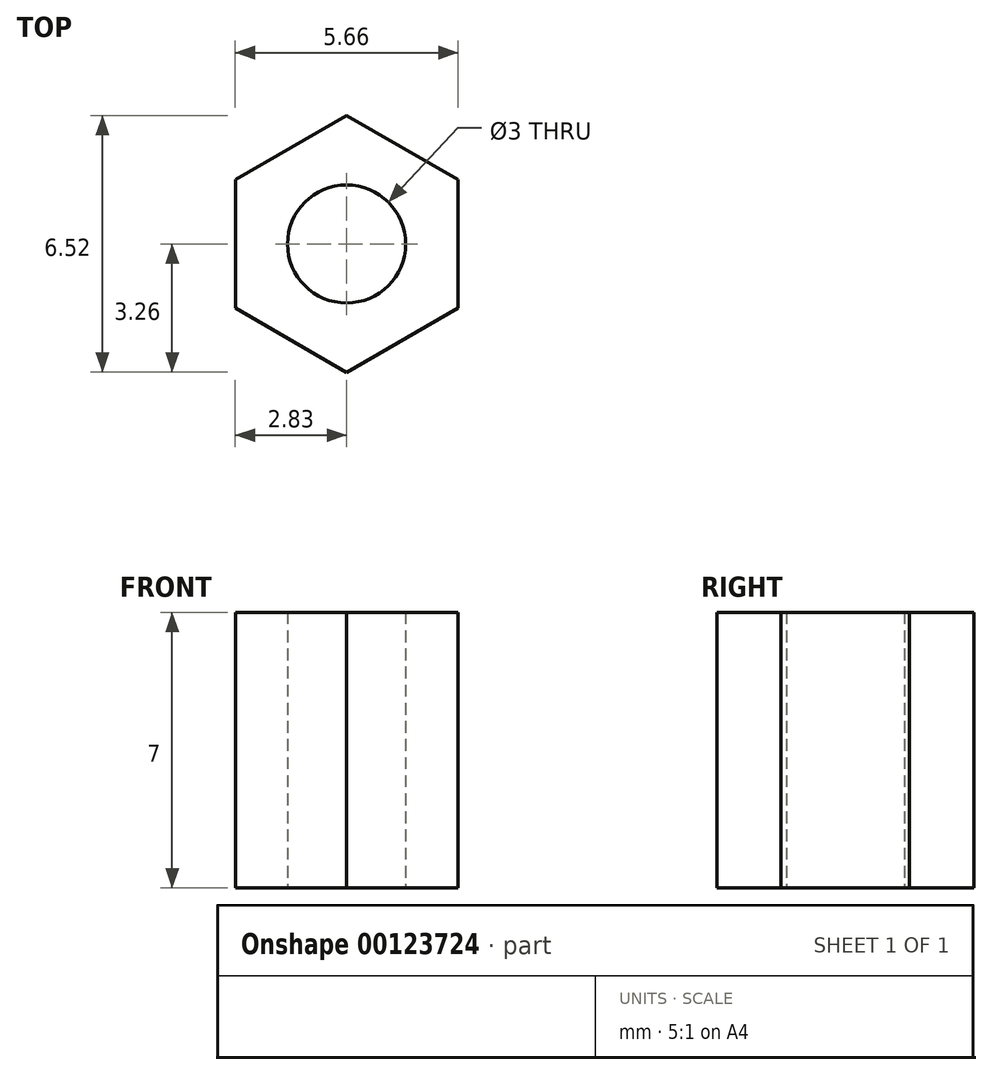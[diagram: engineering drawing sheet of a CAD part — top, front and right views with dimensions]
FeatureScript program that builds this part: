
annotation { "Feature Type Name" : "Feature", "Feature Type Description" : "" }
export const myFeature = defineFeature(function(context is Context, id is Id, definition is map)
    precondition{}
    {
        {
            var Q0;
            Q0=qCreatedBy(makeId("Top.planeOp"),FACE);
            var sketch = newSketch(context, id + "F0", { "sketchPlane" : qUnion([Q0])});
            skCircle(sketch, "E0.cCircle", {"center": v(0, 0) * mm, "radius": 2.83 * mm, "construction": true});
            skLineSegment(sketch, "E0.0", {"start": v(2.83, 1.63) * mm, "end": v(2.83, -1.63) * mm});
            skLineSegment(sketch, "E0.1", {"start": v(2.83, -1.63) * mm, "end": v(0, -3.26) * mm});
            skLineSegment(sketch, "E0.2", {"start": v(0, -3.26) * mm, "end": v(-2.82, -1.63) * mm});
            skLineSegment(sketch, "E0.3", {"start": v(-2.82, -1.63) * mm, "end": v(-2.83, 1.63) * mm});
            skLineSegment(sketch, "E0.4", {"start": v(-2.83, 1.63) * mm, "end": v(0, 3.26) * mm});
            skLineSegment(sketch, "E0.5", {"start": v(0, 3.26) * mm, "end": v(2.83, 1.63) * mm});
            skPoint(sketch, "E0.0.midPoint", {"position": v(2.83, 0) * mm});
            skCircle(sketch, "E1", {"center": v(0, 0) * mm, "radius": 1.5 * mm});
            skSolve(sketch);
        }
        {
            var Q0;
            Q0=qSketchRegion(id+"F0",true);
            extrude(context, id + "F1", {"entities" : qUnion([Q0]), "depth" : 7 * mm});
        }
    });
